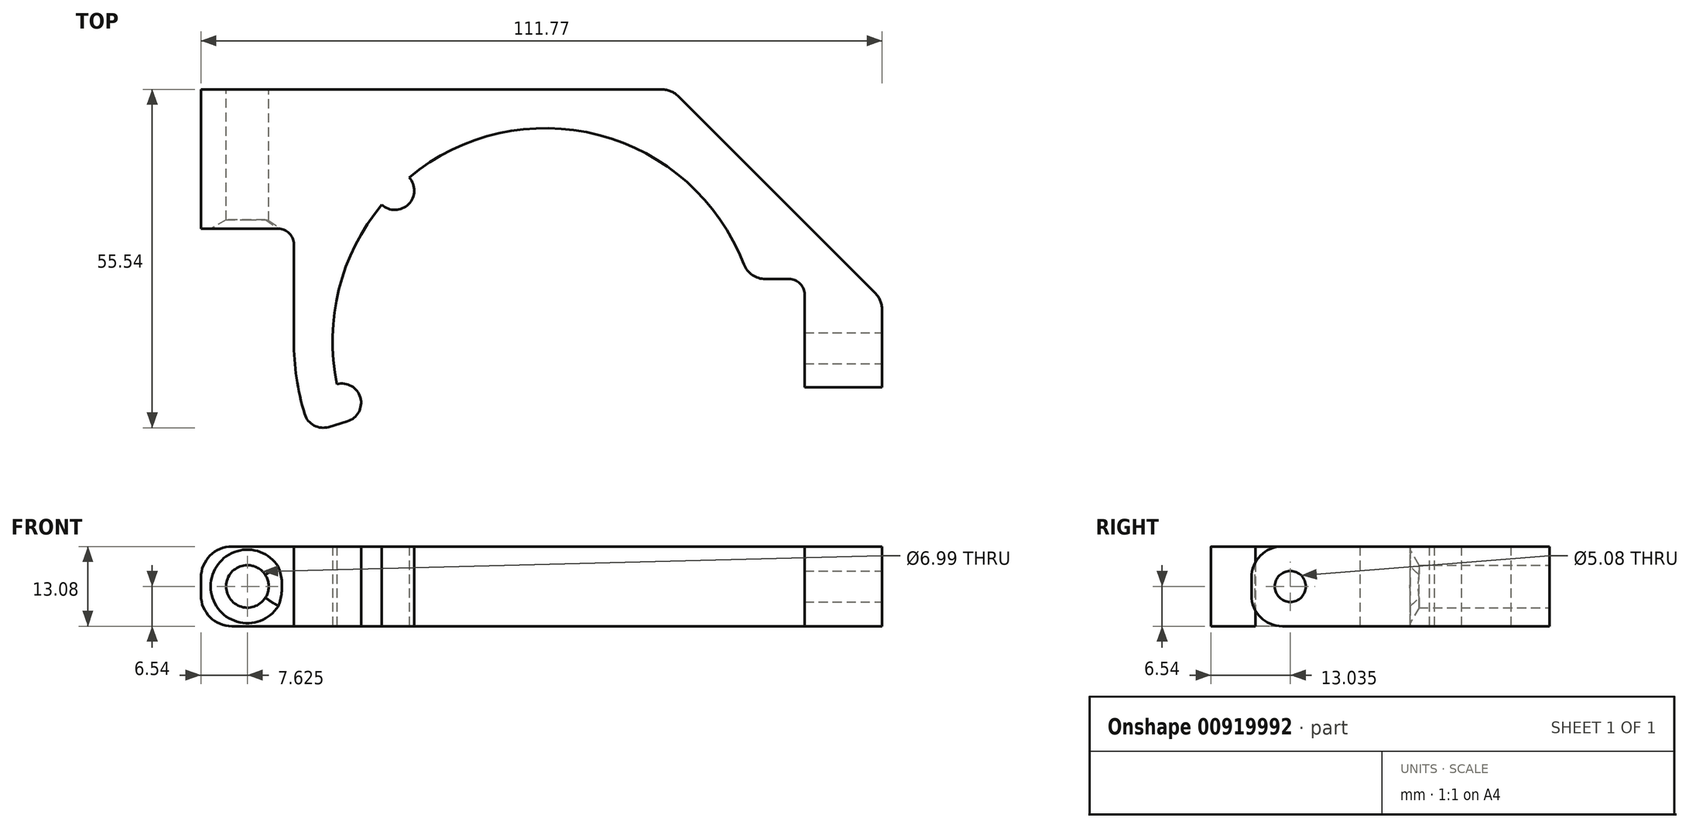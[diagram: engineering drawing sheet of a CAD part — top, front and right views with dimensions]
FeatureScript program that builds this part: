
annotation { "Feature Type Name" : "Feature", "Feature Type Description" : "" }
export const myFeature = defineFeature(function(context is Context, id is Id, definition is map)
    precondition{}
    {
        {
            var Q0;
            Q0=qCreatedBy(makeId("Top.planeOp"),FACE);
            var sketch = newSketch(context, id + "F0", { "sketchPlane" : qUnion([Q0])});
            skCircle(sketch, "E0", {"center": v(0, 0) * mm, "radius": 31.75 * mm, "construction": true});
            skArc(sketch, "E1", {"start": v(32.57, 12.6) * mm, "mid": v(-12.87, 32.47) * mm, "end": v(-32.35, -13.15) * mm});
            skLineSegment(sketch, "E2", {"start": v(0, 41.27) * mm, "end": v(19.14, 41.27) * mm});
            skLineSegment(sketch, "E3", {"start": v(21.83, 40.16) * mm, "end": v(54.13, 7.86) * mm});
            skLineSegment(sketch, "E4", {"start": v(55.25, 5.17) * mm, "end": v(55.25, -7.62) * mm});
            skLineSegment(sketch, "E5", {"start": v(55.25, -7.62) * mm, "end": v(42.55, -7.62) * mm});
            skLineSegment(sketch, "E6", {"start": v(42.55, -7.62) * mm, "end": v(42.55, 7.62) * mm});
            skLineSegment(sketch, "E7", {"start": v(40, 10.16) * mm, "end": v(36.13, 10.16) * mm});
            skLineSegment(sketch, "E8", {"start": v(0, 41.27) * mm, "end": v(-56.51, 41.27) * mm});
            skLineSegment(sketch, "E9", {"start": v(-56.51, 41.27) * mm, "end": v(-56.51, 18.41) * mm});
            skLineSegment(sketch, "E10", {"start": v(-56.51, 18.41) * mm, "end": v(-43.81, 18.41) * mm});
            skLineSegment(sketch, "E11", {"start": v(-41.27, 15.87) * mm, "end": v(-41.27, 0) * mm});
            skArc(sketch, "E12", {"start": v(-41.27, 0) * mm, "mid": v(-40.83, -6.07) * mm, "end": v(-39.49, -12) * mm});
            skArc(sketch, "E13", {"start": v(-39.49, -12) * mm, "mid": v(-35.53, -14.12) * mm, "end": v(-33.41, -10.16) * mm});
            skPoint(sketch, "E14.visualSharp", {"position": v(-41.27, 18.41) * mm});
            skArc(sketch, "E14.filletArc", {"start": v(-41.27, 15.87) * mm, "mid": v(-42.02, 17.67) * mm, "end": v(-43.81, 18.41) * mm});
            skPoint(sketch, "E15.visualSharp", {"position": v(42.55, 10.16) * mm});
            skArc(sketch, "E15.filletArc", {"start": v(42.55, 7.62) * mm, "mid": v(41.8, 9.42) * mm, "end": v(40, 10.16) * mm});
            skPoint(sketch, "E16", {"position": v(42.55, 0) * mm});
            skLineSegment(sketch, "E17", {"start": v(-41.27, 0) * mm, "end": v(0, 0) * mm, "construction": true});
            skLineSegment(sketch, "E18", {"start": v(-33.41, -10.16) * mm, "end": v(33.41, 10.16) * mm, "construction": true});
            skLineSegment(sketch, "E19", {"start": v(0, 0) * mm, "end": v(-24.7, 24.7) * mm, "construction": true});
            skArc(sketch, "E20", {"start": v(-26.84, 22.35) * mm, "mid": v(-22.45, 22.45) * mm, "end": v(-22.35, 26.84) * mm});
            skArc(sketch, "E21", {"start": v(3.17, 34.78) * mm, "mid": v(0, 31.75) * mm, "end": v(-3.17, 34.78) * mm});
            skArc(sketch, "E22", {"start": v(-34.2, -7.08) * mm, "mid": v(-30.24, -10.13) * mm, "end": v(-34.13, -13.25) * mm});
            skLineSegment(sketch, "E23", {"start": v(-35.53, -14.12) * mm, "end": v(-32.5, -13.2) * mm});
            skPoint(sketch, "E24.visualSharp", {"position": v(33.41, 10.16) * mm});
            skArc(sketch, "E24.filletArc", {"start": v(32.57, 12.6) * mm, "mid": v(33.97, 10.83) * mm, "end": v(36.13, 10.16) * mm});
            skPoint(sketch, "E25.visualSharp", {"position": v(55.25, 6.75) * mm});
            skArc(sketch, "E25.filletArc", {"start": v(55.25, 5.17) * mm, "mid": v(54.95, 6.63) * mm, "end": v(54.13, 7.86) * mm});
            skPoint(sketch, "E26.visualSharp", {"position": v(20.72, 41.28) * mm});
            skArc(sketch, "E26.filletArc", {"start": v(21.83, 40.16) * mm, "mid": v(20.6, 40.98) * mm, "end": v(19.14, 41.28) * mm});
            skSolve(sketch);
        }
        {
            var Q0;
            Q0=makeQuery(id+"F0.imprint","IMPRINT",FACE,{"disambiguationData":[TD([[makeQuery(id+"F0.imprint","IMPRINT",EDGE,{"derivedFrom":sQuery(id+"F0.wireOp",EDGE,"E2")}),-1.0]])]});
            var Q1;
            {var subQ0=sQuery(id+"F0.wireOp",EDGE,"E20");Q1=makeQuery(id+"F0.imprint","IMPRINT",FACE,{"disambiguationData":[TD([[makeQuery(id+"F0.imprint","IMPRINT",EDGE,{"derivedFrom":subQ0}),1.0]])]});}
            var Q2;
            {var subQ0=sQuery(id+"F0.wireOp",EDGE,"E1");var subQ1=makeQuery(id+"F0.imprint","INTERSECT",VERTEX,{"derivedFrom":[subQ0,sQuery(id+"F0.wireOp",EDGE,"E13")]});Q2=makeQuery(id+"F0.imprint","IMPRINT",FACE,{"disambiguationData":[TD([[makeQuery(id+"F0.imprint","IMPRINT",EDGE,{"disambiguationData":[TD([[subQ1,1.0]])],"derivedFrom":subQ0}),1.0]])]});}
            var Q3;
            {var subQ0=sQuery(id+"F0.wireOp",EDGE,"E22");var subQ1=sQuery(id+"F0.wireOp",EDGE,"E1");var subQ2=makeQuery(id+"F0.imprint","INTERSECT",VERTEX,{"disambiguationData":[OD(0.0)],"derivedFrom":[subQ1,subQ0]});Q3=makeQuery(id+"F0.imprint","IMPRINT",FACE,{"disambiguationData":[TD([[makeQuery(id+"F0.imprint","IMPRINT",EDGE,{"disambiguationData":[TD([[subQ2,1.0]])],"derivedFrom":subQ1}),-1.0]])]});}
            var Q4;
            {var subQ3=sQuery(id+"F0.wireOp",EDGE,"E23");Q4=makeQuery(id+"F0.imprint","IMPRINT",FACE,{"disambiguationData":[TD([[makeQuery(id+"F0.imprint","IMPRINT",EDGE,{"derivedFrom":subQ3}),1.0]])]});}
            var Q5;
            {var subQ0=sQuery(id+"F0.wireOp",EDGE,"E21");Q5=makeQuery(id+"F0.imprint","IMPRINT",FACE,{"disambiguationData":[TD([[makeQuery(id+"F0.imprint","IMPRINT",EDGE,{"derivedFrom":subQ0}),-1.0]])]});}
            extrude(context, id + "F1", {"entities" : qUnion([Q0, Q1, Q2, Q3, Q4, Q5]), "depth" : 13.08 * mm, "offsetDistance" : 25.4 * mm});
        }
        {
            var Q0;
            Q0=makeQuery(id+"F1.opExtrude","SWEPT_FACE",FACE,{"disambiguationData":[OSD([sQuery(id+"F0.wireOp",EDGE,"E4")])]});
            var sketch = newSketch(context, id + "F2", { "sketchPlane" : qUnion([Q0])});
            skPoint(sketch, "E27", {"position": v(-1.22, 6.54) * mm});
            skPoint(sketch, "E27.positionSnap0", {"position": v(-7.62, 6.54) * mm});
            skPoint(sketch, "E27.positionSnap1", {"position": v(-1.22, 13.08) * mm});
            skCircle(sketch, "E28", {"center": v(-1.22, 6.54) * mm, "radius": 2.54 * mm});
            skSolve(sketch);
        }
        {
            var Q0;
            Q0 = qSketchRegion(id + "F2", true);
            extrude(context, id + "F3", {"entities" : qUnion([Q0]), "operationType" : NewBodyOperationType.REMOVE, "oppositeDirection" : true, "depth" : 25.4 * mm, "offsetDistance" : 25.4 * mm});
        }
        {
            var Q0;
            Q0=makeQuery(id+"F1.opExtrude","SWEPT_FACE",FACE,{"disambiguationData":[OSD([sQuery(id+"F0.wireOp",EDGE,"E2"),sQuery(id+"F0.wireOp",EDGE,"E8")])]});
            var sketch = newSketch(context, id + "F4", { "sketchPlane" : qUnion([Q0])});
            skPoint(sketch, "E29", {"position": v(48.9, 6.54) * mm});
            skPoint(sketch, "E29.positionSnap0", {"position": v(56.51, 6.54) * mm});
            skCircle(sketch, "E30", {"center": v(48.9, 6.54) * mm, "radius": 3.5 * mm});
            skSolve(sketch);
        }
        {
            var Q0;
            Q0=makeQuery(id+"F4.imprint","IMPRINT",FACE,{"disambiguationData":[TD([[makeQuery(id+"F4.imprint","IMPRINT",EDGE,{"derivedFrom":sQuery(id+"F4.wireOp",EDGE,"E30")}),1.0]])]});
            extrude(context, id + "F5", {"entities" : qUnion([Q0]), "operationType" : NewBodyOperationType.REMOVE, "oppositeDirection" : true, "depth" : 25.4 * mm, "offsetDistance" : 25.4 * mm});
        }
        {
            var Q0;
            Q0=makeQuery(id+"F5.boolean.opBoolean","COPY",EDGE,{"derivedFrom":makeQuery(id+"F5.opExtrude","CAP_EDGE",EDGE,{"disambiguationData":[OSD([sQuery(id+"F4.wireOp",EDGE,"E30")])],"isStart":true})});
            var Q1;
            Q1=makeQuery(id+"F5.boolean.opBoolean","INTERSECT",EDGE,{"derivedFrom":[makeQuery(id+"F1.opExtrude","SWEPT_FACE",FACE,{"disambiguationData":[OSD([sQuery(id+"F0.wireOp",EDGE,"E10")])]}),makeQuery(id+"F5.opExtrude","SWEPT_FACE",FACE,{"disambiguationData":[OSD([sQuery(id+"F4.wireOp",EDGE,"E30")])]})]});
            chamfer(context, id + "F6", {"entities" : qUnion([Q0, Q1]), "chamferType" : ChamferType.OFFSET_ANGLE, "width" : 2.54 * mm, "oppositeDirection" : false, "angle" : 30 * degree});
        }
        {
            var Q0;
            Q0=makeQuery(id+"F1.opExtrude","CAP_EDGE",EDGE,{"disambiguationData":[OSD([sQuery(id+"F0.wireOp",EDGE,"E9")])],"isStart":false});
            var Q1;
            Q1=makeQuery(id+"F1.opExtrude","CAP_EDGE",EDGE,{"disambiguationData":[OSD([sQuery(id+"F0.wireOp",EDGE,"E9")])],"isStart":true});
            var Q2;
            Q2=makeQuery(id+"F1.opExtrude","CAP_EDGE",EDGE,{"disambiguationData":[OSD([sQuery(id+"F0.wireOp",EDGE,"E5")])],"isStart":false});
            var Q3;
            Q3=makeQuery(id+"F1.opExtrude","CAP_EDGE",EDGE,{"disambiguationData":[OSD([sQuery(id+"F0.wireOp",EDGE,"E5")])],"isStart":true});
            fillet(context, id + "F7", {"entities" : qUnion([Q0, Q1, Q2, Q3]), "radius" : 5.08 * mm, "tangentPropagation" : true, "allowEdgeOverflow" : false});
        }
    });
